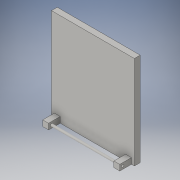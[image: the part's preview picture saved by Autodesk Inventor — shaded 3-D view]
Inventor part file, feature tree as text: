
AUTODESK INVENTOR PART (.ipt)
format: ipt  version: 2016 (Build 200138000, 138)  size: 126,976 bytes
history: native  units: in
note: dims shown in document units (in); Inventor stores cm internally (conversion verified against a paired STEP export)
features: sketch x6, extrude x5, hole x2
ambient origin geometry x8: Origin, YZ Plane, XZ Plane, XY Plane, X Axis, Y Axis, Z Axis, Center Point
bodies: Solid1 (feature_tree)
feature tree (13):
  extrude  "Extrusion1"  Depth=2.0in
  extrude  "Extrusion2"  Depth=0.125in
  extrude  "Extrusion3"  Depth=0.125in
  hole  "Hole1"  [1 undecoded]
  hole  "Hole2"  [1 undecoded]
  extrude  "Extrusion4"  Depth=0.063in
  sketch  "Sketch5"  dims[d10=0.063in d11=0.063in d12=0.05in d13=0.75in d14=0.375in d15=0.25in d16=0.5635in d17=1.0in d18=0.8108in]
  extrude  "Extrusion5"  Depth=1.404in TaperAngle=0.0deg
  sketch  "Sketch1"  dims[d0=1.78in d1=2.0in]
  sketch  "Sketch2"  dims[d2=0.125in d3=0.0in d4=0.125in]
  sketch  "Sketch3"  dims[d5=0.25in d6=0.0in d7=0.125in]
  sketch  "Sketch4"  dims[d8=0.25in d9=0.0in]
  sketch  "Sketch6"  dims[d19=0.063in d33=1.0in d21=0.05in d22=0.75in d23=0.375in d24=0.25in d25=0.5635in d26=1.0in d27=0.8108in d28=1.404in d29=0.0in d30=0.063in d31=0.063in d32=1.404in d34=0.0in]
note: 2 required parameter values undecoded (feature->parameter linkage not recoverable at this tier; creation-order binding heuristic only, values carry confidence <= 0.55)
